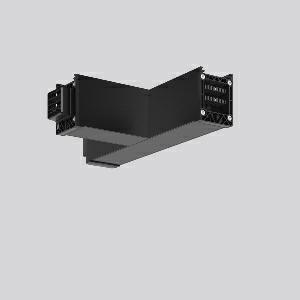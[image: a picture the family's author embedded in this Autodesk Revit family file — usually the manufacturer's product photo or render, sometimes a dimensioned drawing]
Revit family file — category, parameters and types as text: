
# Revit family: linedo_t-verbindung_982774_003_4_1035
name_source: partatom
category: Lighting Fixtures
units: mm (PartAtom-declared; Revit-internal decimal feet)

## family parameters
Cut with Voids When Loaded = No
Host = Face
Light Source = No
Part Type = Normal
Room Calculation Point = No
Round Connector Dimension = Use Diameter
Shared = No

## types (1)
- LINEDO T-Verbindung
    Apparent Load = 0 VA
    Default Elevation = 1800 mm
    Description = Series: LINEDO
T-connector, 7-pole, connection socket / plug - plug. Housing: extruded aluminium profile, powder-coated. Cover made of plastic, surface like housing. LINEDO plug system, plastic, black. Easy connection for rigid or flexible wires. 5 membrane cable entries (2 x M20 and 3 x M25). Suitable for power supply in 7-pole version. Ready prewired. Colour-coded individual cables enable easy electromechanical separation.
Colour: jet black (RAL 9005)
Length: 330 mm
Width: 204 mm
Height: 76 mm
Weight: 940 g
    Height = 76 mm
    Lamp = 0 x
    Length = 331 mm
    Luminous efficacy = 0 lm/W
    Manufacturer = RZB
    ModVariant = No
    Model = 982774.003.4
    Mounting Place = Ceiling
    Mounting Type = Surface mounted
    Number of Poles = 1
    OnlyDefault = Yes
    Power Factor = 1
    Product Name = LINEDO T-Verbindung
    Product group = Surface mounted continuous line luminaire system
    ProductGroupID = 310
    Protection Class = Protection class I
    Protection Degree = Degree of protection
    RLX_Detail_Level = 1
    RLX_Emergency_Light_Flux = 0 lm
    RLX_Emergency_Type = 0
    RLX_Emergency_Type_DB = No
    RlxData = <blob elided: 20349 chars, md5=15fc3a43>
    Standby Power = 0 W
    System Light Flux = 0 lm
    System Power = 0 W
    Type Comments = Product without accessories
    Type Image = 982774.003.jpg
    URL = http://relux.com
    VarID = ---
    Voltage = 0 V
    Weight = 0.00 kg
    Width = 204 mm

## geometry (parser evidence)
native form markers: Blend x4, Sweep x11
no freeform markers — native parametric forms only
